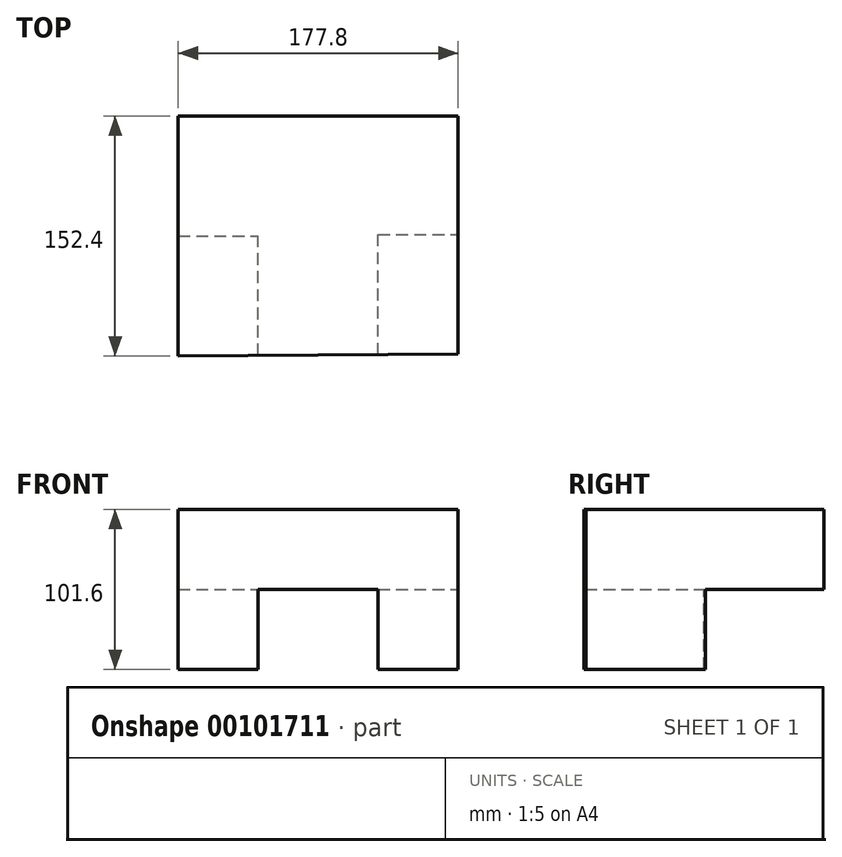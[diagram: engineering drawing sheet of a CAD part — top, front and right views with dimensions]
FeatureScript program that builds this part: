
annotation { "Feature Type Name" : "Feature", "Feature Type Description" : "" }
export const myFeature = defineFeature(function(context is Context, id is Id, definition is map)
    precondition{}
    {
        {
            var Q0;
            Q0=qCreatedBy(makeId("Top.planeOp"),FACE);
            var sketch = newSketch(context, id + "F0", { "sketchPlane" : qUnion([Q0])});
            skLineSegment(sketch, "E0", {"start": v(-87.06, -45.71) * mm, "end": v(-87.06, 106.69) * mm});
            skLineSegment(sketch, "E1", {"start": v(-87.06, 106.69) * mm, "end": v(90.74, 106.69) * mm});
            skLineSegment(sketch, "E2", {"start": v(90.74, 106.69) * mm, "end": v(90.74, -44.55) * mm});
            skLineSegment(sketch, "E3", {"start": v(90.74, -44.55) * mm, "end": v(-87.06, -45.71) * mm});
            skSolve(sketch);
        }
        {
            var Q0;
            Q0=makeQuery(id+"F0.imprint","IMPRINT",FACE,{"disambiguationData":[TD([[makeQuery(id+"F0.imprint","IMPRINT",EDGE,{"derivedFrom":sQuery(id+"F0.wireOp",EDGE,"E0")}),-1.0]])]});
            extrude(context, id + "F1", {"entities" : qUnion([Q0]), "depth" : 50.8 * mm});
        }
        {
            var Q0;
            Q0=makeQuery(id+"F1.opExtrude","CAP_FACE",FACE,{"disambiguationData":[OSD([sQuery(id+"F0.wireOp",EDGE,"E0"),sQuery(id+"F0.wireOp",EDGE,"E1"),sQuery(id+"F0.wireOp",EDGE,"E2"),sQuery(id+"F0.wireOp",EDGE,"E3")])],"isStart":true});
            var sketch = newSketch(context, id + "F2", { "sketchPlane" : qUnion([Q0])});
            skLineSegment(sketch, "E4.bottom", {"start": v(-87.06, 45.71) * mm, "end": v(-36.26, 45.71) * mm});
            skLineSegment(sketch, "E4.top", {"start": v(-87.06, -30.49) * mm, "end": v(-36.26, -30.49) * mm});
            skLineSegment(sketch, "E4.left", {"start": v(-87.06, 45.71) * mm, "end": v(-87.06, -30.49) * mm});
            skLineSegment(sketch, "E4.right", {"start": v(-36.26, 45.71) * mm, "end": v(-36.26, -30.49) * mm});
            skLineSegment(sketch, "E5.bottom", {"start": v(90.74, 44.55) * mm, "end": v(39.94, 44.55) * mm});
            skLineSegment(sketch, "E5.top", {"start": v(90.74, -31.65) * mm, "end": v(39.94, -31.65) * mm});
            skLineSegment(sketch, "E5.left", {"start": v(90.74, 44.55) * mm, "end": v(90.74, -31.65) * mm});
            skLineSegment(sketch, "E5.right", {"start": v(39.94, 44.55) * mm, "end": v(39.94, -31.65) * mm});
            skSolve(sketch);
        }
        {
            var Q0;
            {var subQ0=sQuery(id+"F2.wireOp",EDGE,"E4.top");Q0=makeQuery(id+"F2.imprint","IMPRINT",FACE,{"disambiguationData":[TD([[makeQuery(id+"F2.imprint","IMPRINT",EDGE,{"derivedFrom":subQ0}),1.0]])]});}
            extrude(context, id + "F3", {"entities" : qUnion([Q0]), "operationType" : NewBodyOperationType.ADD, "depth" : 50.8 * mm});
        }
        {
            var Q0;
            Q0=makeQuery(id+"F1.opExtrude","CAP_FACE",FACE,{"disambiguationData":[OSD([sQuery(id+"F0.wireOp",EDGE,"E0"),sQuery(id+"F0.wireOp",EDGE,"E1"),sQuery(id+"F0.wireOp",EDGE,"E2"),sQuery(id+"F0.wireOp",EDGE,"E3")])],"isStart":true});
            var sketch = newSketch(context, id + "F4", { "sketchPlane" : qUnion([Q0])});
            skLineSegment(sketch, "E6.bottom", {"start": v(39.94, 44.88) * mm, "end": v(90.74, 44.88) * mm});
            skLineSegment(sketch, "E6.top", {"start": v(39.94, -31.32) * mm, "end": v(90.74, -31.32) * mm});
            skLineSegment(sketch, "E6.left", {"start": v(39.94, 44.88) * mm, "end": v(39.94, -31.32) * mm});
            skLineSegment(sketch, "E6.right", {"start": v(90.74, 44.88) * mm, "end": v(90.74, -31.32) * mm});
            skSolve(sketch);
        }
        {
            var Q0;
            {var subQ0=sQuery(id+"F4.wireOp",EDGE,"E6.top");Q0=makeQuery(id+"F4.imprint","IMPRINT",FACE,{"disambiguationData":[TD([[makeQuery(id+"F4.imprint","IMPRINT",EDGE,{"derivedFrom":subQ0}),1.0]])]});}
            extrude(context, id + "F5", {"entities" : qUnion([Q0]), "operationType" : NewBodyOperationType.ADD, "depth" : 50.8 * mm});
        }
    });
